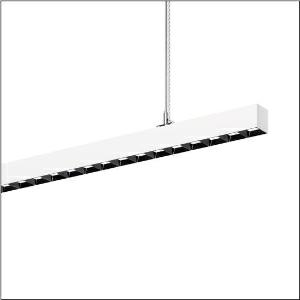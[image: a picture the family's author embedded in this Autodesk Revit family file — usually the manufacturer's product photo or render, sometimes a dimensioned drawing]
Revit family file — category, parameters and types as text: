
# Revit family: silica_r__21_51mx31dc3dwb_5f0e
name_source: partatom
category: Lighting Fixtures
units: mm (PartAtom-declared; Revit-internal decimal feet)

## family parameters
Cut with Voids When Loaded = No
Host = Face
Light Source = No
Part Type = Normal
Room Calculation Point = No
Round Connector Dimension = Use Diameter
Shared = No

## types (1)
- --- (1 x LED, 18230 lm, 113.3 W, 3000K)
    Apparent Load = 113 VA
    CIE Flux Codes = 87 99 100 59 100
    Color Rendering = 80
    Color Temperature = 3000K
    Default Elevation = 1800 mm
    Description = Silica® 21, office luminaire, primary light control with darklight reflector, of PMMA, black, CAT 2 (L<= 3000cd/m²), light emission: direct/indirect distribution, primary light characteristic: symmetric, installation type: suspended mounting, LED, rated luminous flux: 18.230lm, luminous efficacy: 161lm/W, light colour: 830, colour temperature: 3000K, with terminal, 3+2-pole, max. 2.5mm², mains connection: 220..240V, AC, 50/60Hz, rated input power: 113.3W, luminaire housing, of aluminium, traffic white (RAL 9016), length: 3.004mm, width: 53mm, height: 53mm, protection rating (complete): IP20, insulation class (complete): insulation class I (protective earthing), certification: CE, permissible operating ambient temperature: 0..+35°C, standard: EN 50419, packaging unit: 1 piece
    Height = 53 mm
    Lamp = 1 x LED
    Lamp Light Flux = 18230 lm
    Lamp Power = 113.3 W
    Lamp count = 1
    Length = 3004 mm
    Luminous efficacy = 161 lm/W
    Manufacturer = Siteco
    ModVariant = No
    Model = 51MX31DC3DWB
    Mounting Place = Ceiling
    Mounting Type = Pendant
    Number of Poles = 1
    OnlyDefault = Yes
    Power Factor = 1
    Product Name = Silica® 21
    Product group = office luminaire | ceiling pendant
    ProductGroupID = 902
    Protection Class = Protection class I
    Protection Degree = IP 20
    RLX_Detail_Level = 1
    RLX_Emergency_Light_Flux = 0 lm
    RLX_Emergency_Type = 0
    RLX_Emergency_Type_DB = No
    RlxData = <blob elided: 64437 chars, md5=4e9e7a57>
    Socket = socket
    Standby Power = 0 W
    System Light Flux = 18230 lm
    System Power = 113 W
    Type Comments = factory setting: luminous flux: 100 % | dim-lin: 254 | 392 mA
    Type Image = l_1297801.jpg
    URL = http://relux.com
    VarID = @adj_051881
    Voltage = 0 V
    Weight = 0.00 kg
    Width = 53 mm

## geometry (parser evidence)
native form markers: Blend x4, Sweep x14
no freeform markers — native parametric forms only
